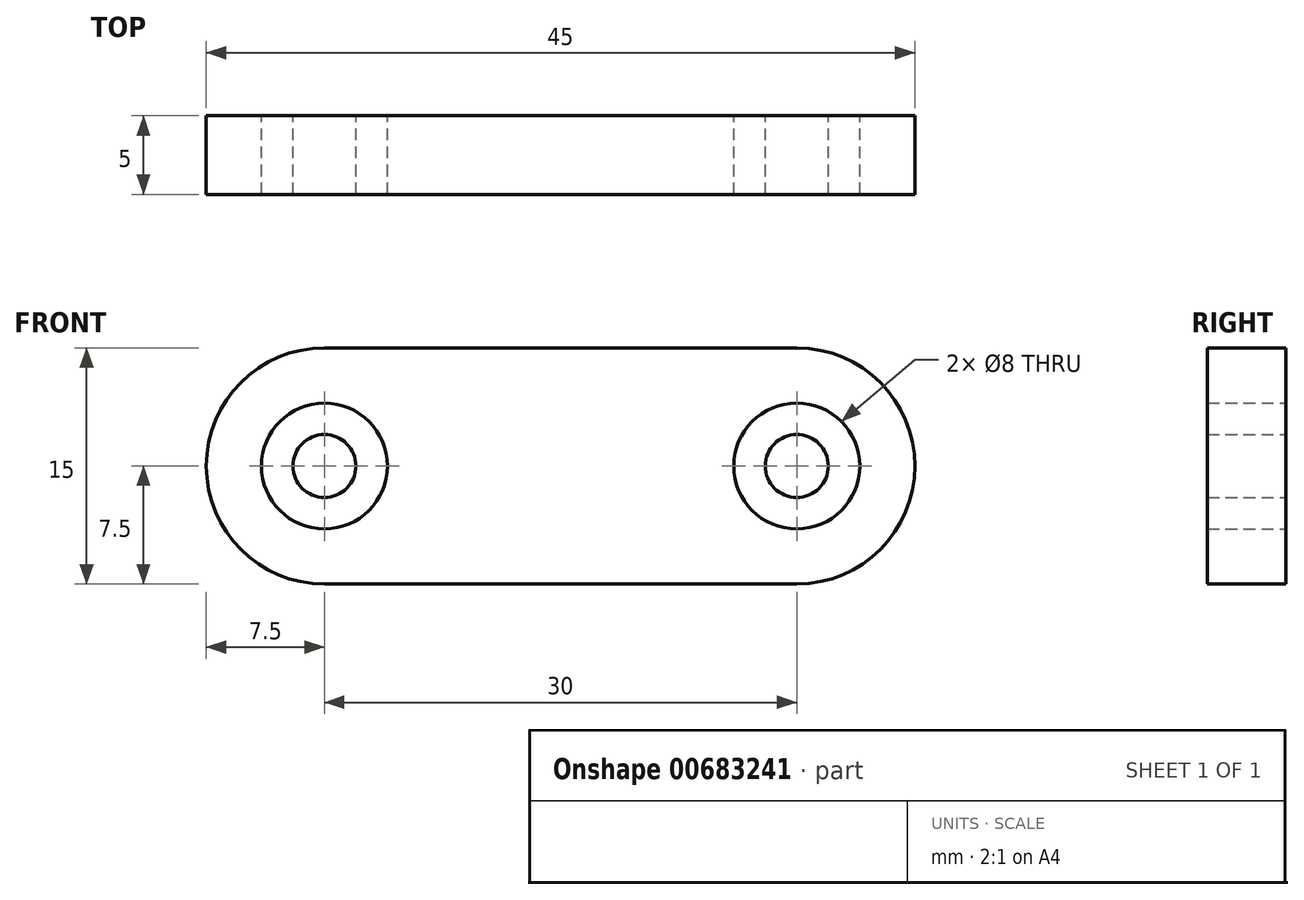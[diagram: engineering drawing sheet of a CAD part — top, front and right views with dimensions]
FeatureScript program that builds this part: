
annotation { "Feature Type Name" : "Feature", "Feature Type Description" : "" }
export const myFeature = defineFeature(function(context is Context, id is Id, definition is map)
    precondition{}
    {
        {
            var Q0;
            Q0=qCreatedBy(makeId("Front.planeOp"),FACE);
            var sketch = newSketch(context, id + "F0", { "sketchPlane" : qUnion([Q0])});
            skLineSegment(sketch, "E0.bottom", {"start": v(0, 0) * mm, "end": v(30, 0) * mm});
            skLineSegment(sketch, "E0.top", {"start": v(0, 15) * mm, "end": v(30, 15) * mm});
            skArc(sketch, "E1", {"start": v(30, 0) * mm, "mid": v(37.5, 7.5) * mm, "end": v(30, 15) * mm});
            skArc(sketch, "E2", {"start": v(0, 15) * mm, "mid": v(-7.5, 7.5) * mm, "end": v(0, 0) * mm});
            skCircle(sketch, "E3", {"center": v(0, 7.5) * mm, "radius": 4 * mm});
            skCircle(sketch, "E4", {"center": v(30, 7.5) * mm, "radius": 4 * mm});
            skCircle(sketch, "E5", {"center": v(30, 7.5) * mm, "radius": 2 * mm});
            skCircle(sketch, "E6", {"center": v(0, 7.5) * mm, "radius": 2 * mm});
            skSolve(sketch);
        }
        {
            var Q0;
            Q0 = qSketchRegion(id + "F0", true);
            var Q1;
            Q1=makeQuery(id+"F0.imprint","IMPRINT",FACE,{"disambiguationData":[TD([[makeQuery(id+"F0.imprint","IMPRINT",EDGE,{"derivedFrom":sQuery(id+"F0.wireOp",EDGE,"E6")}),1.0]])]});
            var Q2;
            Q2=makeQuery(id+"F0.imprint","IMPRINT",FACE,{"disambiguationData":[TD([[makeQuery(id+"F0.imprint","IMPRINT",EDGE,{"derivedFrom":sQuery(id+"F0.wireOp",EDGE,"E5")}),1.0]])]});
            extrude(context, id + "F1", {"entities" : qUnion([Q0, Q1, Q2]), "depth" : 5 * mm, "offsetDistance" : 25 * mm});
        }
    });
